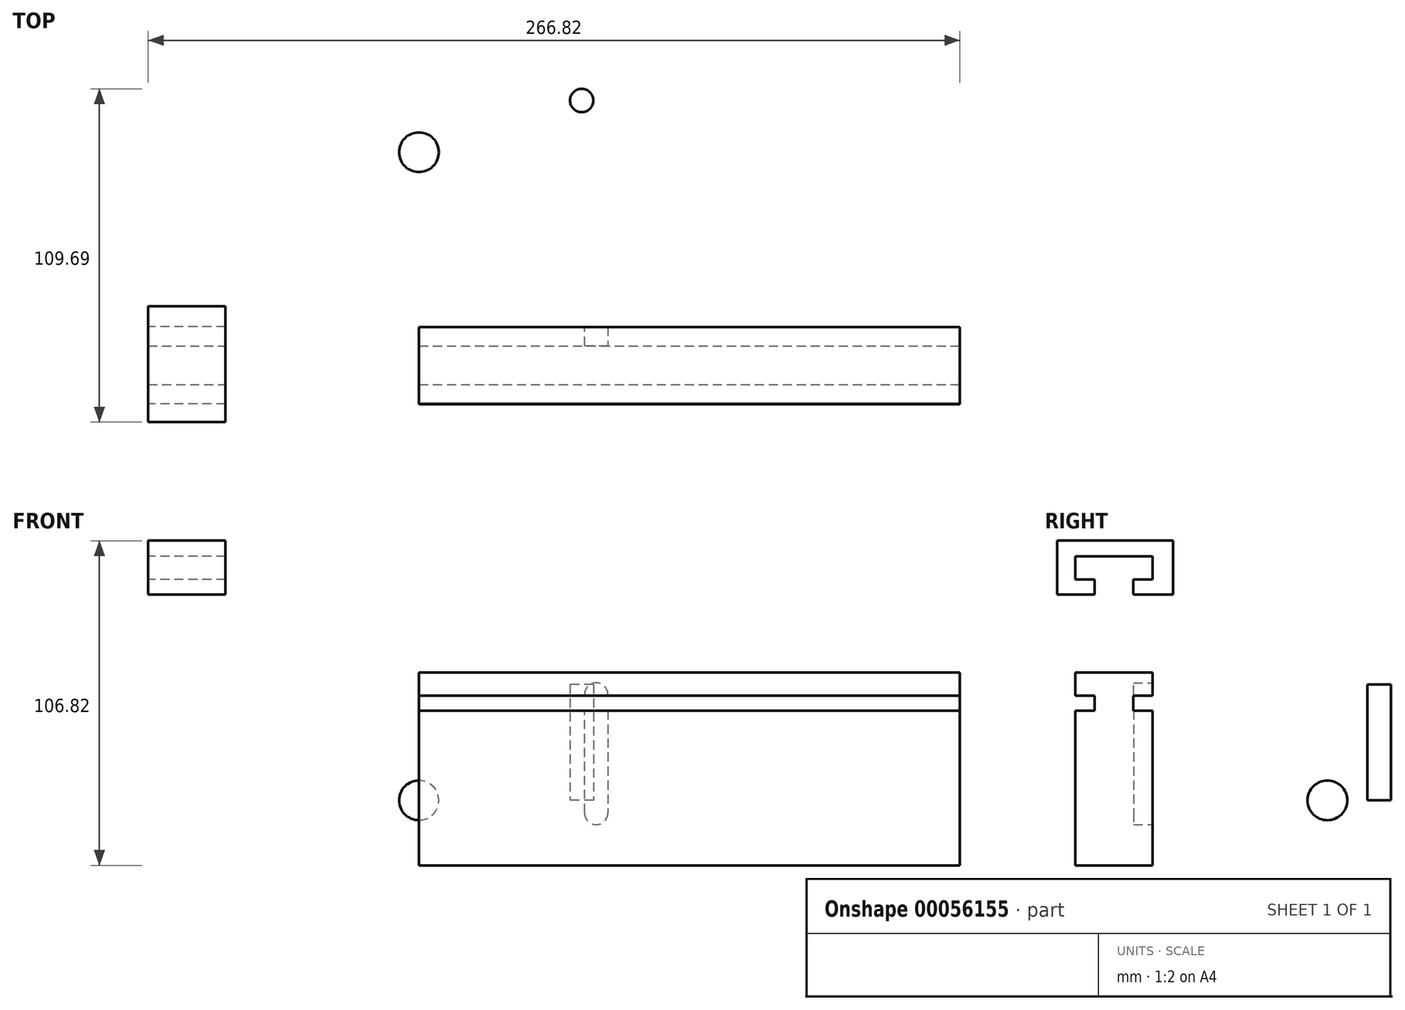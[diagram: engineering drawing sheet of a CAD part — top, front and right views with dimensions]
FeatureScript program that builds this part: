
annotation { "Feature Type Name" : "Feature", "Feature Type Description" : "" }
export const myFeature = defineFeature(function(context is Context, id is Id, definition is map)
    precondition{}
    {
        {
            var Q0;
            Q0=qCreatedBy(makeId("Right.planeOp"),FACE);
            var sketch = newSketch(context, id + "F0", { "sketchPlane" : qUnion([Q0])});
            skLineSegment(sketch, "E0.bottom", {"start": v(-46.62, 42.1) * mm, "end": v(-21.22, 42.1) * mm});
            skLineSegment(sketch, "E0.top", {"start": v(-46.62, -21.4) * mm, "end": v(-21.22, -21.4) * mm});
            skLineSegment(sketch, "E0.left", {"start": v(-46.62, 42.1) * mm, "end": v(-46.62, -21.4) * mm});
            skLineSegment(sketch, "E0.right", {"start": v(-21.22, 42.1) * mm, "end": v(-21.22, -21.4) * mm});
            skSolve(sketch);
        }
        {
            var Q0;
            Q0=makeQuery(id+"F0.imprint","IMPRINT",FACE,{"disambiguationData":[TD([[makeQuery(id+"F0.imprint","IMPRINT",EDGE,{"derivedFrom":sQuery(id+"F0.wireOp",EDGE,"E0.bottom")}),-1.0]])]});
            extrude(context, id + "F1", {"entities" : qUnion([Q0]), "depth" : 177.8 * mm});
        }
        {
            var Q0;
            Q0=qCreatedBy(makeId("Right.planeOp"),FACE);
            var sketch = newSketch(context, id + "F2", { "sketchPlane" : qUnion([Q0])});
            skLineSegment(sketch, "E1.rect.bottom", {"start": v(-52.7, 51.66) * mm, "end": v(-14.6, 51.66) * mm});
            skLineSegment(sketch, "E1.rect.top", {"start": v(-52.7, 33.88) * mm, "end": v(-14.6, 33.88) * mm});
            skLineSegment(sketch, "E1.rect.left", {"start": v(-52.7, 51.66) * mm, "end": v(-52.7, 33.88) * mm});
            skLineSegment(sketch, "E1.rect.right", {"start": v(-14.6, 51.66) * mm, "end": v(-14.6, 33.88) * mm});
            skPoint(sketch, "E1.rect.middle", {"position": v(-33.66, 42.77) * mm});
            skSolve(sketch);
        }
        {
            var Q0;
            Q0 = qSketchRegion(id + "F2", true);
            extrude(context, id + "F3", {"entities" : qUnion([Q0]), "depth" : 25.4 * mm});
        }
        {
            var Q0;
            Q0=makeQuery(id+"F3.opExtrude","SWEPT_BODY",BODY,{"disambiguationData":[OSD([sQuery(id+"F2.wireOp",EDGE,"E1.rect.bottom"),sQuery(id+"F2.wireOp",EDGE,"E1.rect.top"),sQuery(id+"F2.wireOp",EDGE,"E1.rect.left"),sQuery(id+"F2.wireOp",EDGE,"E1.rect.right")])]});
            transform(context, id + "F4", {"entities" : qUnion([Q0]), "transformType" : TransformType.TRANSLATION_3D, "dx" : 0 * mm, "dy" : -51.7 * mm, "dz" : 1.05 * mm, "makeCopy" : false});
        }
        {
            var Q0;
            Q0=makeQuery(id+"F3.opExtrude","CAP_FACE",FACE,{"disambiguationData":[OSD([sQuery(id+"F2.wireOp",EDGE,"E1.rect.bottom"),sQuery(id+"F2.wireOp",EDGE,"E1.rect.top"),sQuery(id+"F2.wireOp",EDGE,"E1.rect.left"),sQuery(id+"F2.wireOp",EDGE,"E1.rect.right")])],"isStart":true});
            var sketch = newSketch(context, id + "F5", { "sketchPlane" : qUnion([Q0])});
            skLineSegment(sketch, "E2.bottom", {"start": v(73.03, 47.54) * mm, "end": v(98.43, 47.54) * mm});
            skLineSegment(sketch, "E2.top", {"start": v(73.03, 39.92) * mm, "end": v(98.43, 39.92) * mm});
            skLineSegment(sketch, "E2.left", {"start": v(73.03, 47.54) * mm, "end": v(73.03, 39.92) * mm});
            skLineSegment(sketch, "E2.right", {"start": v(98.43, 47.54) * mm, "end": v(98.43, 39.92) * mm});
            skSolve(sketch);
        }
        {
            var Q0;
            Q0=makeQuery(id+"F5.imprint","IMPRINT",FACE,{"disambiguationData":[TD([[makeQuery(id+"F5.imprint","IMPRINT",EDGE,{"derivedFrom":sQuery(id+"F5.wireOp",EDGE,"E2.bottom")}),-1.0]])]});
            extrude(context, id + "F6", {"entities" : qUnion([Q0]), "operationType" : NewBodyOperationType.REMOVE, "oppositeDirection" : true, "depth" : 41.28 * mm});
        }
        {
            var Q0;
            Q0=makeQuery(id+"F3.opExtrude","CAP_FACE",FACE,{"disambiguationData":[OSD([sQuery(id+"F2.wireOp",EDGE,"E1.rect.bottom"),sQuery(id+"F2.wireOp",EDGE,"E1.rect.top"),sQuery(id+"F2.wireOp",EDGE,"E1.rect.left"),sQuery(id+"F2.wireOp",EDGE,"E1.rect.right")])],"isStart":true});
            var sketch = newSketch(context, id + "F7", { "sketchPlane" : qUnion([Q0])});
            skLineSegment(sketch, "E3.bottom", {"start": v(73.03, 44.88) * mm, "end": v(85.73, 44.88) * mm});
            skLineSegment(sketch, "E3.top", {"start": v(73.03, 37.26) * mm, "end": v(85.73, 37.26) * mm});
            skLineSegment(sketch, "E3.left", {"start": v(73.03, 44.88) * mm, "end": v(73.03, 37.26) * mm});
            skLineSegment(sketch, "E3.right", {"start": v(85.73, 44.88) * mm, "end": v(85.73, 37.26) * mm});
            skSolve(sketch);
        }
        {
            var Q0;
            {var subQ0=sQuery(id+"F7.wireOp",EDGE,"E3.bottom");Q0=makeQuery(id+"F7.imprint","IMPRINT",FACE,{"disambiguationData":[TD([[makeQuery(id+"F7.imprint","IMPRINT",EDGE,{"derivedFrom":subQ0}),-1.0]])]});}
            var Q1;
            {var subQ0=sQuery(id+"F7.wireOp",EDGE,"E3.top");Q1=makeQuery(id+"F7.imprint","IMPRINT",FACE,{"disambiguationData":[TD([[makeQuery(id+"F7.imprint","IMPRINT",EDGE,{"derivedFrom":subQ0}),1.0]])]});}
            extrude(context, id + "F8", {"entities" : qUnion([Q0, Q1]), "depth" : 38.1 * mm});
        }
        {
            var Q0;
            Q0=makeQuery(id+"F8.opExtrude","SWEPT_BODY",BODY,{"disambiguationData":[OSD([sQuery(id+"F7.wireOp",EDGE,"E3.bottom"),sQuery(id+"F7.wireOp",EDGE,"E3.top"),sQuery(id+"F7.wireOp",EDGE,"E3.left"),sQuery(id+"F7.wireOp",EDGE,"E3.right")])]});
            transform(context, id + "F9", {"entities" : qUnion([Q0]), "transformType" : TransformType.TRANSLATION_3D, "dx" : 0 * mm, "dy" : -6.35 * mm, "dz" : -3.54 * mm, "makeCopy" : false});
        }
        {
            var Q0;
            Q0=makeQuery(id+"F8.opExtrude","SWEPT_BODY",BODY,{"disambiguationData":[OSD([sQuery(id+"F7.wireOp",EDGE,"E3.bottom"),sQuery(id+"F7.wireOp",EDGE,"E3.top"),sQuery(id+"F7.wireOp",EDGE,"E3.left"),sQuery(id+"F7.wireOp",EDGE,"E3.right")])]});
            transform(context, id + "F10", {"entities" : qUnion([Q0]), "transformType" : TransformType.TRANSLATION_3D, "dx" : 36.05 * mm, "dy" : 0 * mm, "dz" : 0 * mm, "makeCopy" : false});
        }
        {
            var Q0;
            Q0=makeQuery(id+"F8.opExtrude","SWEPT_BODY",BODY,{"disambiguationData":[OSD([sQuery(id+"F7.wireOp",EDGE,"E3.bottom"),sQuery(id+"F7.wireOp",EDGE,"E3.top"),sQuery(id+"F7.wireOp",EDGE,"E3.left"),sQuery(id+"F7.wireOp",EDGE,"E3.right")])]});
            var Q1;
            Q1=makeQuery(id+"F3.opExtrude","SWEPT_BODY",BODY,{"disambiguationData":[OSD([sQuery(id+"F2.wireOp",EDGE,"E1.rect.bottom"),sQuery(id+"F2.wireOp",EDGE,"E1.rect.top"),sQuery(id+"F2.wireOp",EDGE,"E1.rect.left"),sQuery(id+"F2.wireOp",EDGE,"E1.rect.right")])]});
            booleanBodies(context, id + "F11", {"operationType" : BooleanOperationType.SUBTRACTION, "tools" : qUnion([Q0]), "targets" : qUnion([Q1])});
        }
        {
            var Q0;
            Q0=makeQuery(id+"F3.opExtrude","SWEPT_BODY",BODY,{"disambiguationData":[OSD([sQuery(id+"F2.wireOp",EDGE,"E1.rect.bottom"),sQuery(id+"F2.wireOp",EDGE,"E1.rect.top"),sQuery(id+"F2.wireOp",EDGE,"E1.rect.left"),sQuery(id+"F2.wireOp",EDGE,"E1.rect.right")])]});
            transform(context, id + "F12", {"entities" : qUnion([Q0]), "transformType" : TransformType.TRANSLATION_3D, "dx" : 0 * mm, "dy" : 51.86 * mm, "dz" : -5.42 * mm, "makeCopy" : false});
        }
        {
            var Q0;
            Q0=makeQuery(id+"F3.opExtrude","SWEPT_BODY",BODY,{"disambiguationData":[OSD([sQuery(id+"F2.wireOp",EDGE,"E1.rect.bottom"),sQuery(id+"F2.wireOp",EDGE,"E1.rect.top"),sQuery(id+"F2.wireOp",EDGE,"E1.rect.left"),sQuery(id+"F2.wireOp",EDGE,"E1.rect.right")])]});
            transform(context, id + "F13", {"entities" : qUnion([Q0]), "transformType" : TransformType.TRANSLATION_3D, "dx" : 177.8 * mm, "dy" : 0 * mm, "dz" : 0 * mm, "makeCopy" : true});
        }
        {
            var Q0;
            Q0=makeQuery(id+"F3.opExtrude","SWEPT_BODY",BODY,{"disambiguationData":[OSD([sQuery(id+"F2.wireOp",EDGE,"E1.rect.bottom"),sQuery(id+"F2.wireOp",EDGE,"E1.rect.top"),sQuery(id+"F2.wireOp",EDGE,"E1.rect.left"),sQuery(id+"F2.wireOp",EDGE,"E1.rect.right")])]});
            var Q1;
            Q1=makeQuery(id+"F1.opExtrude","CAP_EDGE",EDGE,{"disambiguationData":[OSD([sQuery(id+"F0.wireOp",EDGE,"E0.left")])],"isStart":true});
            transform(context, id + "F14", {"entities" : qUnion([Q0]), "transformType" : TransformType.TRANSLATION_3D, "dx" : -89.02 * mm, "dy" : 0 * mm, "dz" : 38.15 * mm, "makeCopy" : false});
        }
        {
            var Q0;
            Q0=makeQuery(id+"F13.opPattern","COPY",BODY,{"derivedFrom":makeQuery(id+"F3.opExtrude","SWEPT_BODY",BODY,{"disambiguationData":[OSD([sQuery(id+"F2.wireOp",EDGE,"E1.rect.bottom"),sQuery(id+"F2.wireOp",EDGE,"E1.rect.top"),sQuery(id+"F2.wireOp",EDGE,"E1.rect.left"),sQuery(id+"F2.wireOp",EDGE,"E1.rect.right")])]}),"instanceName":"1"});
            transform(context, id + "F15", {"entities" : qUnion([Q0]), "transformType" : TransformType.TRANSLATION_3D, "dx" : 9.13 * mm, "dy" : 0 * mm, "dz" : 0 * mm, "makeCopy" : false});
        }
        {
            var Q0;
            Q0=makeQuery(id+"F13.opPattern","COPY",FACE,{"derivedFrom":makeQuery(id+"F3.opExtrude","CAP_FACE",FACE,{"disambiguationData":[OSD([sQuery(id+"F2.wireOp",EDGE,"E1.rect.bottom"),sQuery(id+"F2.wireOp",EDGE,"E1.rect.top"),sQuery(id+"F2.wireOp",EDGE,"E1.rect.left"),sQuery(id+"F2.wireOp",EDGE,"E1.rect.right")])],"isStart":true}),"instanceName":"1"});
            extrude(context, id + "F16", {"entities" : qUnion([Q0]), "depth" : 231.78 * mm});
        }
        {
            var Q0;
            Q0=makeQuery(id+"F13.opPattern","COPY",BODY,{"derivedFrom":makeQuery(id+"F3.opExtrude","SWEPT_BODY",BODY,{"disambiguationData":[OSD([sQuery(id+"F2.wireOp",EDGE,"E1.rect.bottom"),sQuery(id+"F2.wireOp",EDGE,"E1.rect.top"),sQuery(id+"F2.wireOp",EDGE,"E1.rect.left"),sQuery(id+"F2.wireOp",EDGE,"E1.rect.right")])]}),"instanceName":"1"});
            var Q1;
            Q1=makeQuery(id+"F1.opExtrude","SWEPT_BODY",BODY,{"disambiguationData":[OSD([sQuery(id+"F0.wireOp",EDGE,"E0.bottom"),sQuery(id+"F0.wireOp",EDGE,"E0.top"),sQuery(id+"F0.wireOp",EDGE,"E0.left"),sQuery(id+"F0.wireOp",EDGE,"E0.right")])]});
            booleanBodies(context, id + "F17", {"operationType" : BooleanOperationType.SUBTRACTION, "tools" : qUnion([Q0]), "targets" : qUnion([Q1])});
        }
        {
            var Q0;
            Q0=makeQuery(id+"F16.opExtrude","SWEPT_BODY",BODY,{"disambiguationData":[OSD([sQuery(id+"F2.wireOp",EDGE,"E1.rect.bottom"),sQuery(id+"F2.wireOp",EDGE,"E1.rect.top"),sQuery(id+"F2.wireOp",EDGE,"E1.rect.left"),sQuery(id+"F2.wireOp",EDGE,"E1.rect.right")])]});
            var Q1;
            Q1=makeQuery(id+"F1.opExtrude","SWEPT_BODY",BODY,{"disambiguationData":[OSD([sQuery(id+"F0.wireOp",EDGE,"E0.bottom"),sQuery(id+"F0.wireOp",EDGE,"E0.top"),sQuery(id+"F0.wireOp",EDGE,"E0.left"),sQuery(id+"F0.wireOp",EDGE,"E0.right")])]});
            booleanBodies(context, id + "F18", {"operationType" : BooleanOperationType.SUBTRACTION, "tools" : qUnion([Q0]), "targets" : qUnion([Q1])});
        }
        {
            var Q0;
            Q0=qCreatedBy(makeId("Front.planeOp"),FACE);
            var sketch = newSketch(context, id + "F19", { "sketchPlane" : qUnion([Q0])});
            skArc(sketch, "E4", {"start": v(62.11, 34.83) * mm, "mid": v(58.26, 38.67) * mm, "end": v(54.41, 34.83) * mm});
            skArc(sketch, "E5", {"start": v(54.41, -4.13) * mm, "mid": v(58.26, -7.98) * mm, "end": v(62.11, -4.13) * mm});
            skLineSegment(sketch, "E6", {"start": v(62.11, 34.83) * mm, "end": v(62.11, -4.13) * mm});
            skLineSegment(sketch, "E7", {"start": v(54.41, -4.13) * mm, "end": v(54.41, 34.83) * mm});
            skSolve(sketch);
        }
        {
            var Q0;
            {var subQ0=sQuery(id+"F19.wireOp",EDGE,"E4");Q0=makeQuery(id+"F19.imprint","IMPRINT",FACE,{"disambiguationData":[TD([[makeQuery(id+"F19.imprint","IMPRINT",EDGE,{"derivedFrom":subQ0}),1.0]])]});}
            extrude(context, id + "F20", {"entities" : qUnion([Q0]), "operationType" : NewBodyOperationType.REMOVE, "depth" : 27.43 * mm});
        }
        {
            var Q0;
            Q0=qCreatedBy(makeId("Top.planeOp"),FACE);
            var sketch = newSketch(context, id + "F21", { "sketchPlane" : qUnion([Q0])});
            skCircle(sketch, "E8", {"center": v(53.5, 53.29) * mm, "radius": 3.85 * mm});
            skSolve(sketch);
        }
        {
            var Q0;
            Q0=makeQuery(id+"F21.imprint","IMPRINT",FACE,{"disambiguationData":[TD([[makeQuery(id+"F21.imprint","IMPRINT",EDGE,{"derivedFrom":sQuery(id+"F21.wireOp",EDGE,"E8")}),1.0]])]});
            extrude(context, id + "F22", {"entities" : qUnion([Q0]), "depth" : 38.1 * mm});
        }
        {
            var Q0;
            Q0=qCreatedBy(makeId("Right.planeOp"),FACE);
            var sketch = newSketch(context, id + "F23", { "sketchPlane" : qUnion([Q0])});
            skArc(sketch, "E9", {"start": v(29.74, 0) * mm, "mid": v(36.27, -6.53) * mm, "end": v(42.8, 0) * mm});
            skLineSegment(sketch, "E10", {"start": v(42.8, 0) * mm, "end": v(29.74, 0) * mm});
            skSolve(sketch);
        }
        {
            var Q0;
            Q0=makeQuery(id+"F23.imprint","IMPRINT",FACE,{"disambiguationData":[TD([[makeQuery(id+"F23.imprint","IMPRINT",EDGE,{"derivedFrom":sQuery(id+"F23.wireOp",EDGE,"E9")}),1.0]])]});
            var Q1;
            Q1=sQuery(id+"F23.wireOp",EDGE,"E10");
            revolve(context, id + "F24", {"entities" : qUnion([Q0]), "axis" : qUnion([Q1]), "revolveType" : RevolveType.FULL});
        }
    });
